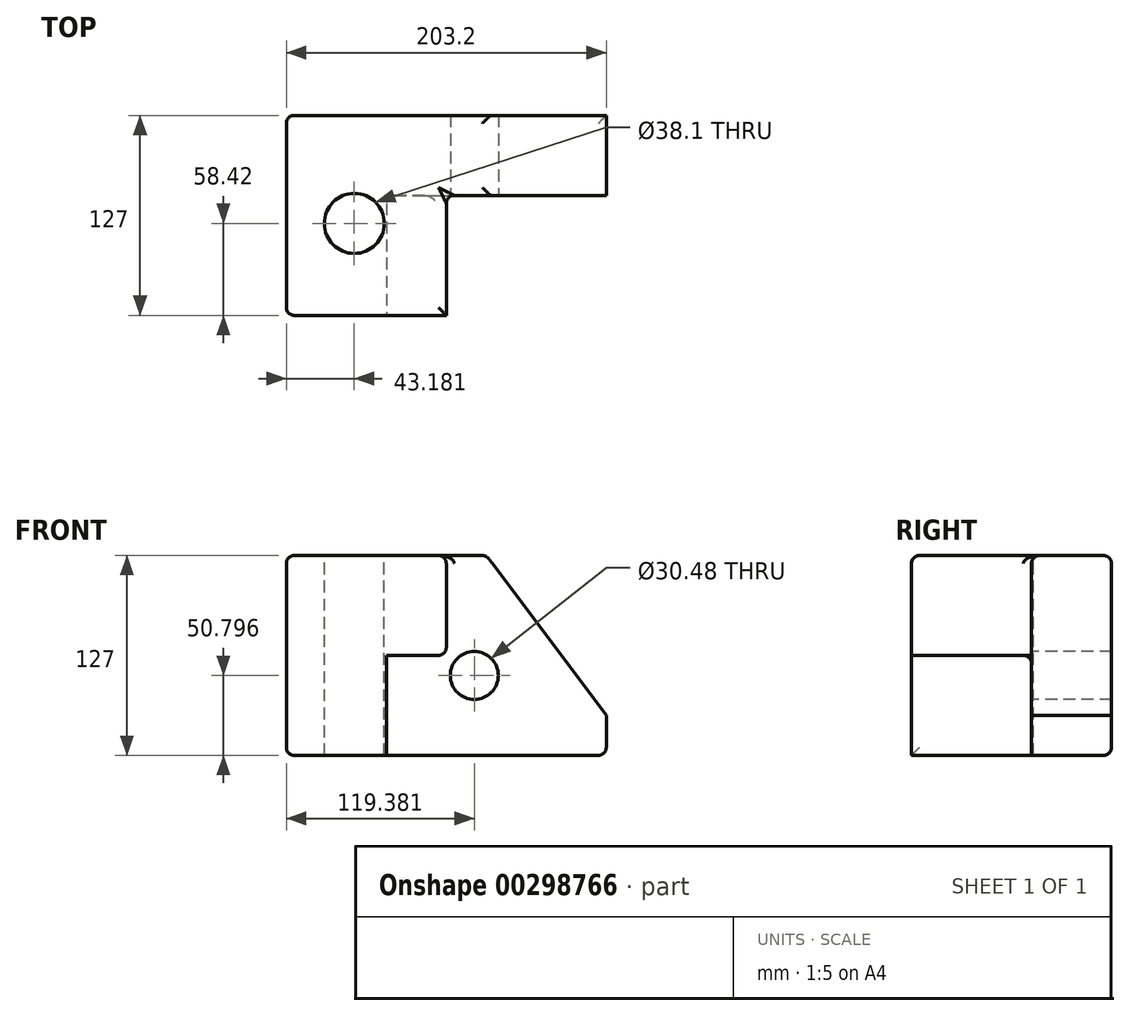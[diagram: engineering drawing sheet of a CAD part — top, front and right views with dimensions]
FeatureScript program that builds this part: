
annotation { "Feature Type Name" : "Feature", "Feature Type Description" : "" }
export const myFeature = defineFeature(function(context is Context, id is Id, definition is map)
    precondition{}
    {
        {
            var Q0;
            Q0=qCreatedBy(makeId("Front.planeOp"),FACE);
            var sketch = newSketch(context, id + "F0", { "sketchPlane" : qUnion([Q0])});
            skLineSegment(sketch, "E0.bottom", {"start": v(-90.35, 62.2) * mm, "end": v(112.85, 62.2) * mm});
            skLineSegment(sketch, "E0.top", {"start": v(-90.35, -64.8) * mm, "end": v(112.85, -64.8) * mm});
            skLineSegment(sketch, "E0.left", {"start": v(-90.35, 62.2) * mm, "end": v(-90.35, -64.8) * mm});
            skLineSegment(sketch, "E0.right", {"start": v(112.85, 62.2) * mm, "end": v(112.85, -64.8) * mm});
            skSolve(sketch);
        }
        {
            var Q0;
            Q0=makeQuery(id+"F0.imprint","IMPRINT",FACE,{"disambiguationData":[TD([[makeQuery(id+"F0.imprint","IMPRINT",EDGE,{"derivedFrom":sQuery(id+"F0.wireOp",EDGE,"E0.bottom")}),-1.0]])]});
            extrude(context, id + "F1", {"entities" : qUnion([Q0]), "depth" : 127 * mm});
        }
        {
            var Q0;
            Q0=makeQuery(id+"F1.opExtrude","CAP_FACE",FACE,{"disambiguationData":[OSD([sQuery(id+"F0.wireOp",EDGE,"E0.bottom"),sQuery(id+"F0.wireOp",EDGE,"E0.top"),sQuery(id+"F0.wireOp",EDGE,"E0.left"),sQuery(id+"F0.wireOp",EDGE,"E0.right")])],"isStart":false});
            var sketch = newSketch(context, id + "F2", { "sketchPlane" : qUnion([Q0])});
            skLineSegment(sketch, "E1", {"start": v(-90.35, -64.8) * mm, "end": v(-90.35, 62.2) * mm});
            skLineSegment(sketch, "E2", {"start": v(-90.35, 62.2) * mm, "end": v(11.25, 62.2) * mm});
            skLineSegment(sketch, "E3", {"start": v(11.25, 62.2) * mm, "end": v(11.25, -1.3) * mm});
            skLineSegment(sketch, "E4", {"start": v(11.25, -1.3) * mm, "end": v(-26.85, -1.3) * mm});
            skLineSegment(sketch, "E5", {"start": v(-26.85, -1.3) * mm, "end": v(-26.85, -64.8) * mm});
            skLineSegment(sketch, "E6", {"start": v(-26.85, -64.8) * mm, "end": v(-90.35, -64.8) * mm});
            skSolve(sketch);
        }
        {
            var Q0;
            {var subQ2=sQuery(id+"F2.wireOp",EDGE,"E3");Q0=makeQuery(id+"F2.imprint","IMPRINT",FACE,{"disambiguationData":[TD([[makeQuery(id+"F2.imprint","IMPRINT",EDGE,{"derivedFrom":subQ2}),1.0]])]});}
            extrude(context, id + "F3", {"entities" : qUnion([Q0]), "operationType" : NewBodyOperationType.REMOVE, "oppositeDirection" : true, "depth" : 76.2 * mm});
        }
        {
            var Q0;
            Q0=makeQuery(id+"F1.opExtrude","SWEPT_EDGE",EDGE,{"disambiguationData":[OSD([sQuery(id+"F0.wireOp",EDGE,"E0.bottom"),sQuery(id+"F0.wireOp",EDGE,"E0.right")])]});
            chamfer(context, id + "F4", {"entities" : qUnion([Q0]), "chamferType" : ChamferType.TWO_OFFSETS, "width1" : 76.2 * mm, "oppositeDirection" : false, "width2" : 101.6 * mm, "tangentPropagation" : true});
        }
        {
            var Q0;
            Q0=makeQuery(id+"F1.opExtrude","SWEPT_FACE",FACE,{"disambiguationData":[OSD([sQuery(id+"F0.wireOp",EDGE,"E0.bottom")])]});
            fillet(context, id + "F5", {"entities" : qUnion([Q0]), "radius" : 5.08 * mm, "tangentPropagation" : true, "allowEdgeOverflow" : false});
        }
        {
            var Q0;
            Q0=makeQuery(id+"F3.boolean.opBoolean","COPY",EDGE,{"derivedFrom":makeQuery(id+"F3.opExtrude","CAP_EDGE",EDGE,{"disambiguationData":[OSD([sQuery(id+"F2.wireOp",EDGE,"E3")])],"isStart":true})});
            var Q1;
            Q1=makeQuery(id+"F3.boolean.opBoolean","COPY",EDGE,{"derivedFrom":makeQuery(id+"F3.opExtrude","SWEPT_EDGE",EDGE,{"disambiguationData":[OSD([sQuery(id+"F2.wireOp",EDGE,"E3"),sQuery(id+"F2.wireOp",EDGE,"E4")])]})});
            var Q2;
            Q2=makeQuery(id+"F3.boolean.opBoolean","COPY",EDGE,{"derivedFrom":makeQuery(id+"F3.opExtrude","CAP_EDGE",EDGE,{"disambiguationData":[OSD([sQuery(id+"F2.wireOp",EDGE,"E4")])],"isStart":true})});
            var Q3;
            Q3=makeQuery(id+"F3.boolean.opBoolean","COPY",EDGE,{"derivedFrom":makeQuery(id+"F3.opExtrude","CAP_EDGE",EDGE,{"disambiguationData":[OSD([sQuery(id+"F2.wireOp",EDGE,"E5")])],"isStart":true})});
            var Q4;
            Q4=makeQuery(id+"F1.opExtrude","CAP_EDGE",EDGE,{"disambiguationData":[OSD([sQuery(id+"F0.wireOp",EDGE,"E0.left")])],"isStart":false});
            var Q5;
            Q5=makeQuery(id+"F1.opExtrude","CAP_EDGE",EDGE,{"disambiguationData":[OSD([sQuery(id+"F0.wireOp",EDGE,"E0.left")])],"isStart":true});
            var Q6;
            Q6=makeQuery(id+"F1.opExtrude","SWEPT_EDGE",EDGE,{"disambiguationData":[OSD([sQuery(id+"F0.wireOp",EDGE,"E0.top"),sQuery(id+"F0.wireOp",EDGE,"E0.left")])]});
            var Q7;
            Q7=makeQuery(id+"F1.opExtrude","CAP_EDGE",EDGE,{"disambiguationData":[OSD([sQuery(id+"F0.wireOp",EDGE,"E0.top")])],"isStart":true});
            var Q8;
            Q8=makeQuery(id+"F3.boolean.opBoolean","COPY",EDGE,{"derivedFrom":makeQuery(id+"F3.opExtrude","SWEPT_EDGE",EDGE,{"disambiguationData":[OSD([sQuery(id+"F0.wireOp",EDGE,"E0.top"),sQuery(id+"F2.wireOp",EDGE,"E5"),sQuery(id+"F2.wireOp",EDGE,"E6")])]})});
            var Q9;
            Q9=makeQuery(id+"F3.boolean.opBoolean","COPY",EDGE,{"derivedFrom":makeQuery(id+"F3.opExtrude","CAP_EDGE",EDGE,{"disambiguationData":[OSD([sQuery(id+"F0.wireOp",EDGE,"E0.top")])],"isStart":false})});
            var Q10;
            Q10=makeQuery(id+"F1.opExtrude","SWEPT_EDGE",EDGE,{"disambiguationData":[OSD([sQuery(id+"F0.wireOp",EDGE,"E0.top"),sQuery(id+"F0.wireOp",EDGE,"E0.right")])]});
            var Q11;
            Q11=makeQuery(id+"F3.boolean.opBoolean","COPY",EDGE,{"derivedFrom":makeQuery(id+"F3.opExtrude","CAP_EDGE",EDGE,{"disambiguationData":[OSD([sQuery(id+"F2.wireOp",EDGE,"E3")])],"isStart":false})});
            var Q12;
            Q12=makeQuery(id+"F3.boolean.opBoolean","COPY",EDGE,{"derivedFrom":makeQuery(id+"F3.opExtrude","CAP_EDGE",EDGE,{"disambiguationData":[OSD([sQuery(id+"F2.wireOp",EDGE,"E5")])],"isStart":false})});
            fillet(context, id + "F6", {"entities" : qUnion([Q0, Q1, Q2, Q3, Q4, Q5, Q6, Q7, Q8, Q9, Q10, Q11, Q12]), "radius" : 5.08 * mm, "tangentPropagation" : true, "allowEdgeOverflow" : false});
        }
        {
            var Q0;
            Q0=makeQuery(id+"F3.boolean.opBoolean","COPY",FACE,{"derivedFrom":makeQuery(id+"F3.opExtrude","CAP_FACE",FACE,{"disambiguationData":[OSD([sQuery(id+"F0.wireOp",EDGE,"E0.bottom"),sQuery(id+"F0.wireOp",EDGE,"E0.top"),sQuery(id+"F0.wireOp",EDGE,"E0.right"),sQuery(id+"F2.wireOp",EDGE,"E3"),sQuery(id+"F2.wireOp",EDGE,"E4"),sQuery(id+"F2.wireOp",EDGE,"E5")])],"isStart":false})});
            var sketch = newSketch(context, id + "F7", { "sketchPlane" : qUnion([Q0])});
            skCircle(sketch, "E7", {"center": v(29.03, -14) * mm, "radius": 15.24 * mm});
            skSolve(sketch);
        }
        {
            var Q0;
            Q0=makeQuery(id+"F7.imprint","IMPRINT",FACE,{"disambiguationData":[TD([[makeQuery(id+"F7.imprint","IMPRINT",EDGE,{"derivedFrom":sQuery(id+"F7.wireOp",EDGE,"E7")}),1.0]])]});
            var Q1;
            Q1=makeQuery(id+"F1.opExtrude","CAP_FACE",FACE,{"disambiguationData":[OSD([sQuery(id+"F0.wireOp",EDGE,"E0.bottom"),sQuery(id+"F0.wireOp",EDGE,"E0.top"),sQuery(id+"F0.wireOp",EDGE,"E0.left"),sQuery(id+"F0.wireOp",EDGE,"E0.right")])],"isStart":true});
            extrude(context, id + "F8", {"entities" : qUnion([Q0]), "operationType" : NewBodyOperationType.REMOVE, "endBound" : BoundingType.UP_TO_SURFACE, "oppositeDirection" : true, "endBoundEntityFace" : qUnion([Q1]), "depth" : 25.4 * mm});
        }
        {
            var Q0;
            Q0=makeQuery(id+"F1.opExtrude","SWEPT_FACE",FACE,{"disambiguationData":[OSD([sQuery(id+"F0.wireOp",EDGE,"E0.bottom")])]});
            var sketch = newSketch(context, id + "F9", { "sketchPlane" : qUnion([Q0])});
            skCircle(sketch, "E8", {"center": v(-47.17, -68.58) * mm, "radius": 19.05 * mm});
            skSolve(sketch);
        }
        {
            var Q0;
            Q0 = qSketchRegion(id + "F9", true);
            var Q1;
            Q1=makeQuery(id+"F1.opExtrude","SWEPT_FACE",FACE,{"disambiguationData":[OSD([sQuery(id+"F0.wireOp",EDGE,"E0.top")])]});
            extrude(context, id + "F10", {"entities" : qUnion([Q0]), "operationType" : NewBodyOperationType.REMOVE, "endBound" : BoundingType.UP_TO_SURFACE, "oppositeDirection" : true, "endBoundEntityFace" : qUnion([Q1]), "depth" : 25.4 * mm});
        }
    });
